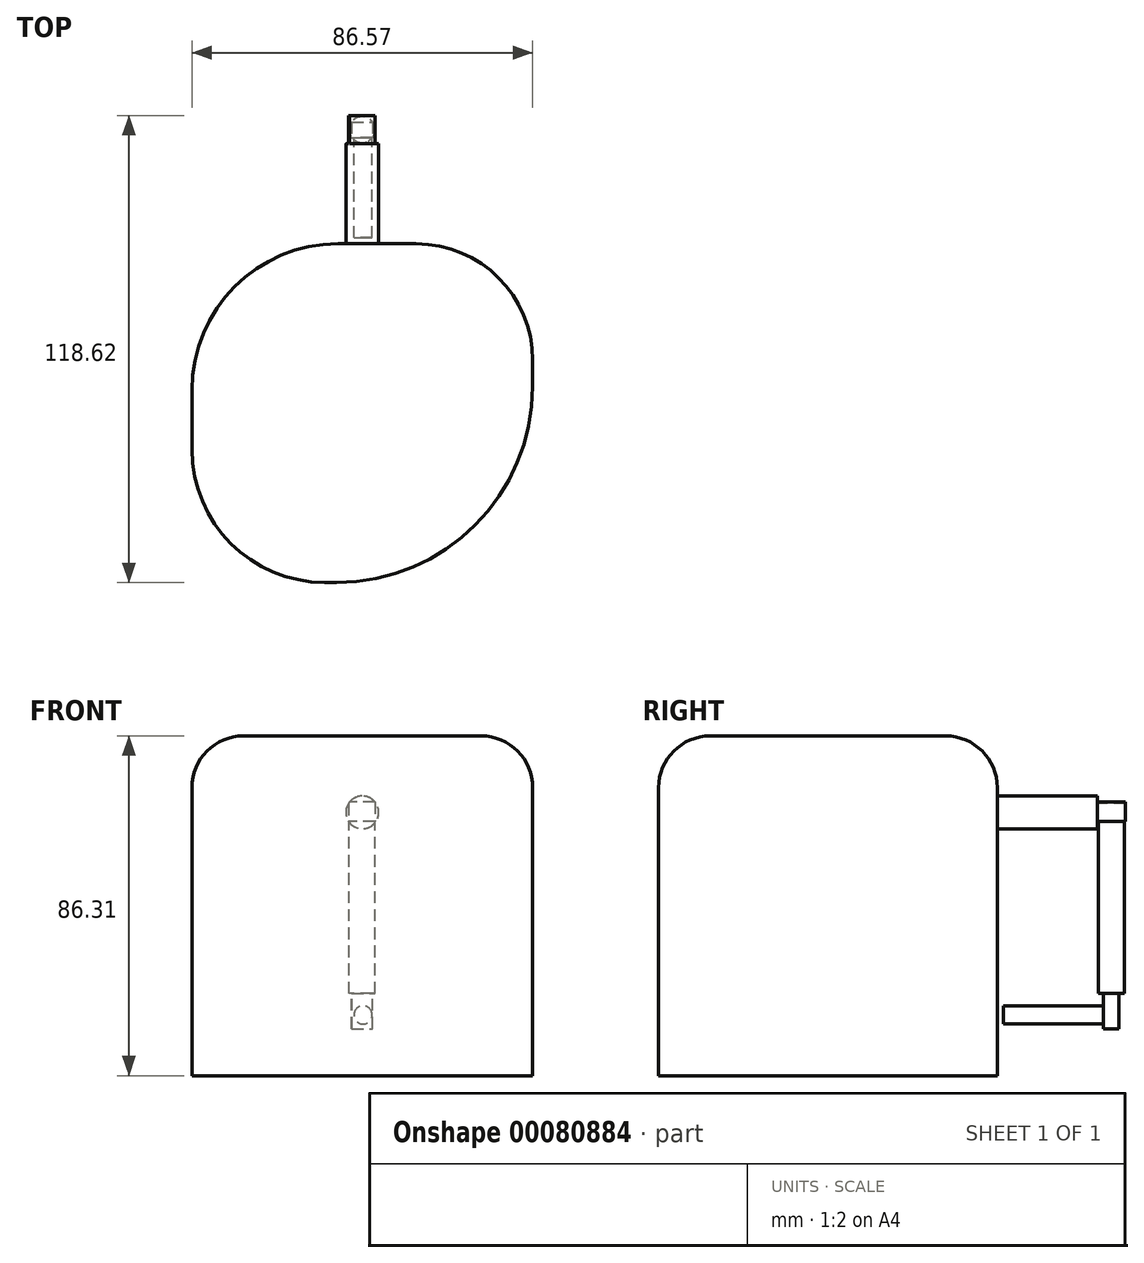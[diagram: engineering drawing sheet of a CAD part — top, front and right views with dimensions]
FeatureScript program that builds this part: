
annotation { "Feature Type Name" : "Feature", "Feature Type Description" : "" }
export const myFeature = defineFeature(function(context is Context, id is Id, definition is map)
    precondition{}
    {
        {
            var Q0;
            Q0=qCreatedBy(makeId("Top.planeOp"),FACE);
            var sketch = newSketch(context, id + "F0", { "sketchPlane" : qUnion([Q0])});
            skLineSegment(sketch, "E0.bottom", {"start": v(-39.78, 35.47) * mm, "end": v(46.8, 35.47) * mm});
            skLineSegment(sketch, "E0.top", {"start": v(-39.78, -50.58) * mm, "end": v(46.8, -50.58) * mm});
            skLineSegment(sketch, "E0.left", {"start": v(-39.78, 35.47) * mm, "end": v(-39.78, -50.58) * mm});
            skLineSegment(sketch, "E0.right", {"start": v(46.8, 35.47) * mm, "end": v(46.8, -50.58) * mm});
            skSolve(sketch);
        }
        {
            var Q0;
            Q0=makeQuery(id+"F0.imprint","IMPRINT",FACE,{"disambiguationData":[TD([[makeQuery(id+"F0.imprint","IMPRINT",EDGE,{"derivedFrom":sQuery(id+"F0.wireOp",EDGE,"E0.bottom")}),-1.0]])]});
            extrude(context, id + "F1", {"entities" : qUnion([Q0]), "depth" : 86.31 * mm});
        }
        {
            var Q0;
            Q0=makeQuery(id+"F1.opExtrude","SWEPT_FACE",FACE,{"disambiguationData":[OSD([sQuery(id+"F0.wireOp",EDGE,"E0.bottom")])]});
            var sketch = newSketch(context, id + "F2", { "sketchPlane" : qUnion([Q0])});
            skCircle(sketch, "E1", {"center": v(-3.5, 66.88) * mm, "radius": 4.17 * mm});
            skPoint(sketch, "E1.centerSnap0", {"position": v(-3.5, 86.31) * mm});
            skSolve(sketch);
        }
        {
            var Q0;
            Q0=makeQuery(id+"F2.imprint","IMPRINT",FACE,{"disambiguationData":[TD([[makeQuery(id+"F2.imprint","IMPRINT",EDGE,{"derivedFrom":sQuery(id+"F2.wireOp",EDGE,"E1")}),1.0]])]});
            extrude(context, id + "F3", {"entities" : qUnion([Q0]), "operationType" : NewBodyOperationType.ADD, "depth" : 25.4 * mm});
        }
        {
            var Q0;
            Q0=makeQuery(id+"F3.opExtrude","CAP_FACE",FACE,{"disambiguationData":[OSD([sQuery(id+"F2.wireOp",EDGE,"E1")])],"isStart":false});
            var sketch = newSketch(context, id + "F4", { "sketchPlane" : qUnion([Q0])});
            skLineSegment(sketch, "E2.bottom", {"start": v(-6.76, 69.5) * mm, "end": v(0, 69.5) * mm});
            skLineSegment(sketch, "E2.top", {"start": v(-6.76, 64.62) * mm, "end": v(0, 64.62) * mm});
            skLineSegment(sketch, "E2.left", {"start": v(-6.76, 69.5) * mm, "end": v(-6.76, 64.62) * mm});
            skLineSegment(sketch, "E2.right", {"start": v(0, 69.5) * mm, "end": v(0, 64.62) * mm});
            skSolve(sketch);
        }
        {
            var Q0;
            {var subQ1=sQuery(id+"F4.wireOp",EDGE,"E2.top");Q0=makeQuery(id+"F4.imprint","IMPRINT",FACE,{"disambiguationData":[TD([[makeQuery(id+"F4.imprint","IMPRINT",EDGE,{"derivedFrom":subQ1}),1.0]])]});}
            extrude(context, id + "F5", {"entities" : qUnion([Q0]), "operationType" : NewBodyOperationType.ADD, "depth" : 7.17 * mm});
        }
        {
            var Q0;
            Q0=makeQuery(id+"F5.opExtrude","SWEPT_FACE",FACE,{"disambiguationData":[OSD([sQuery(id+"F4.wireOp",EDGE,"E2.top")])]});
            var sketch = newSketch(context, id + "F6", { "sketchPlane" : qUnion([Q0])});
            skCircle(sketch, "E3", {"center": v(3.45, -64.45) * mm, "radius": 3.3 * mm});
            skPoint(sketch, "E3.centerSnap0", {"position": v(6.76, -64.45) * mm});
            skSolve(sketch);
        }
        {
            var Q0;
            Q0=makeQuery(id+"F6.imprint","IMPRINT",FACE,{"disambiguationData":[TD([[makeQuery(id+"F6.imprint","IMPRINT",EDGE,{"derivedFrom":sQuery(id+"F6.wireOp",EDGE,"E3")}),1.0]])]});
            extrude(context, id + "F7", {"entities" : qUnion([Q0]), "operationType" : NewBodyOperationType.ADD, "depth" : 43.74 * mm});
        }
        {
            var Q0;
            Q0=makeQuery(id+"F7.opExtrude","CAP_FACE",FACE,{"disambiguationData":[OSD([sQuery(id+"F6.wireOp",EDGE,"E3")])],"isStart":false});
            var sketch = newSketch(context, id + "F8", { "sketchPlane" : qUnion([Q0])});
            skLineSegment(sketch, "E4.bottom", {"start": v(0.77, -66.4) * mm, "end": v(6.05, -66.4) * mm});
            skLineSegment(sketch, "E4.top", {"start": v(0.77, -62.4) * mm, "end": v(6.05, -62.4) * mm});
            skLineSegment(sketch, "E4.left", {"start": v(0.77, -66.4) * mm, "end": v(0.77, -62.4) * mm});
            skLineSegment(sketch, "E4.right", {"start": v(6.05, -66.4) * mm, "end": v(6.05, -62.4) * mm});
            skSolve(sketch);
        }
        {
            var Q0;
            {var subQ2=sQuery(id+"F8.wireOp",EDGE,"E4.bottom");Q0=makeQuery(id+"F8.imprint","IMPRINT",FACE,{"disambiguationData":[TD([[makeQuery(id+"F8.imprint","IMPRINT",EDGE,{"derivedFrom":subQ2}),1.0]])]});}
            extrude(context, id + "F9", {"entities" : qUnion([Q0]), "operationType" : NewBodyOperationType.ADD, "depth" : 8.94 * mm});
        }
        {
            var Q0;
            Q0=makeQuery(id+"F9.opExtrude","SWEPT_FACE",FACE,{"disambiguationData":[OSD([sQuery(id+"F8.wireOp",EDGE,"E4.top")])]});
            var sketch = newSketch(context, id + "F10", { "sketchPlane" : qUnion([Q0])});
            skCircle(sketch, "E5", {"center": v(3.7, 15.42) * mm, "radius": 2.32 * mm});
            skSolve(sketch);
        }
        {
            var Q0;
            Q0=makeQuery(id+"F10.imprint","IMPRINT",FACE,{"disambiguationData":[TD([[makeQuery(id+"F10.imprint","IMPRINT",EDGE,{"derivedFrom":sQuery(id+"F10.wireOp",EDGE,"E5")}),1.0]])]});
            extrude(context, id + "F11", {"entities" : qUnion([Q0]), "operationType" : NewBodyOperationType.ADD, "depth" : 25.4 * mm});
        }
        {
            var Q0;
            Q0=makeQuery(id+"F1.opExtrude","CAP_FACE",FACE,{"disambiguationData":[OSD([sQuery(id+"F0.wireOp",EDGE,"E0.bottom"),sQuery(id+"F0.wireOp",EDGE,"E0.top"),sQuery(id+"F0.wireOp",EDGE,"E0.left"),sQuery(id+"F0.wireOp",EDGE,"E0.right")])],"isStart":false});
            fillet(context, id + "F12", {"entities" : qUnion([Q0]), "radius" : 13.12 * mm, "tangentPropagation" : true, "allowEdgeOverflow" : false});
        }
        {
            var Q0;
            Q0=makeQuery(id+"F1.opExtrude","SWEPT_EDGE",EDGE,{"disambiguationData":[OSD([sQuery(id+"F0.wireOp",EDGE,"E0.bottom"),sQuery(id+"F0.wireOp",EDGE,"E0.right")])]});
            fillet(context, id + "F13", {"entities" : qUnion([Q0]), "radius" : 29.57 * mm, "tangentPropagation" : true, "allowEdgeOverflow" : false});
        }
        {
            var Q0;
            Q0=makeQuery(id+"F1.opExtrude","SWEPT_EDGE",EDGE,{"disambiguationData":[OSD([sQuery(id+"F0.wireOp",EDGE,"E0.bottom"),sQuery(id+"F0.wireOp",EDGE,"E0.left")])]});
            fillet(context, id + "F14", {"entities" : qUnion([Q0]), "radius" : 37.17 * mm, "tangentPropagation" : true, "allowEdgeOverflow" : false});
        }
        {
            var Q0;
            Q0=makeQuery(id+"F1.opExtrude","SWEPT_EDGE",EDGE,{"disambiguationData":[OSD([sQuery(id+"F0.wireOp",EDGE,"E0.top"),sQuery(id+"F0.wireOp",EDGE,"E0.right")])]});
            fillet(context, id + "F15", {"entities" : qUnion([Q0]), "radius" : 49.82 * mm, "tangentPropagation" : true, "allowEdgeOverflow" : false});
        }
        {
            var Q0;
            Q0=makeQuery(id+"F1.opExtrude","SWEPT_EDGE",EDGE,{"disambiguationData":[OSD([sQuery(id+"F0.wireOp",EDGE,"E0.top"),sQuery(id+"F0.wireOp",EDGE,"E0.left")])]});
            fillet(context, id + "F16", {"entities" : qUnion([Q0]), "radius" : 33.77 * mm, "tangentPropagation" : true, "allowEdgeOverflow" : false});
        }
    });
